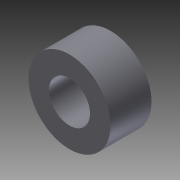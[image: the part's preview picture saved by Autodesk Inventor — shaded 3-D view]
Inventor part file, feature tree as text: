
AUTODESK INVENTOR PART (.ipt)
format: ipt  version: 2014 SP1 (Build 180222100, 222)  size: 79,872 bytes
history: native  units: in
note: dims shown in document units (in); Inventor stores cm internally (conversion verified against a paired STEP export)
features: extrude x1, sketch x1
ambient origin geometry x8: Origin, YZ Plane, XZ Plane, XY Plane, X Axis, Y Axis, Z Axis, Center Point
bodies: Solid1 (feature_tree)
feature tree (2):
  extrude  "Extrusion1"  Depth=0.25in
  sketch  "Sketch1"  dims[d0=0.5in d1=0.25in d2=0.25in d3=0.0in]
